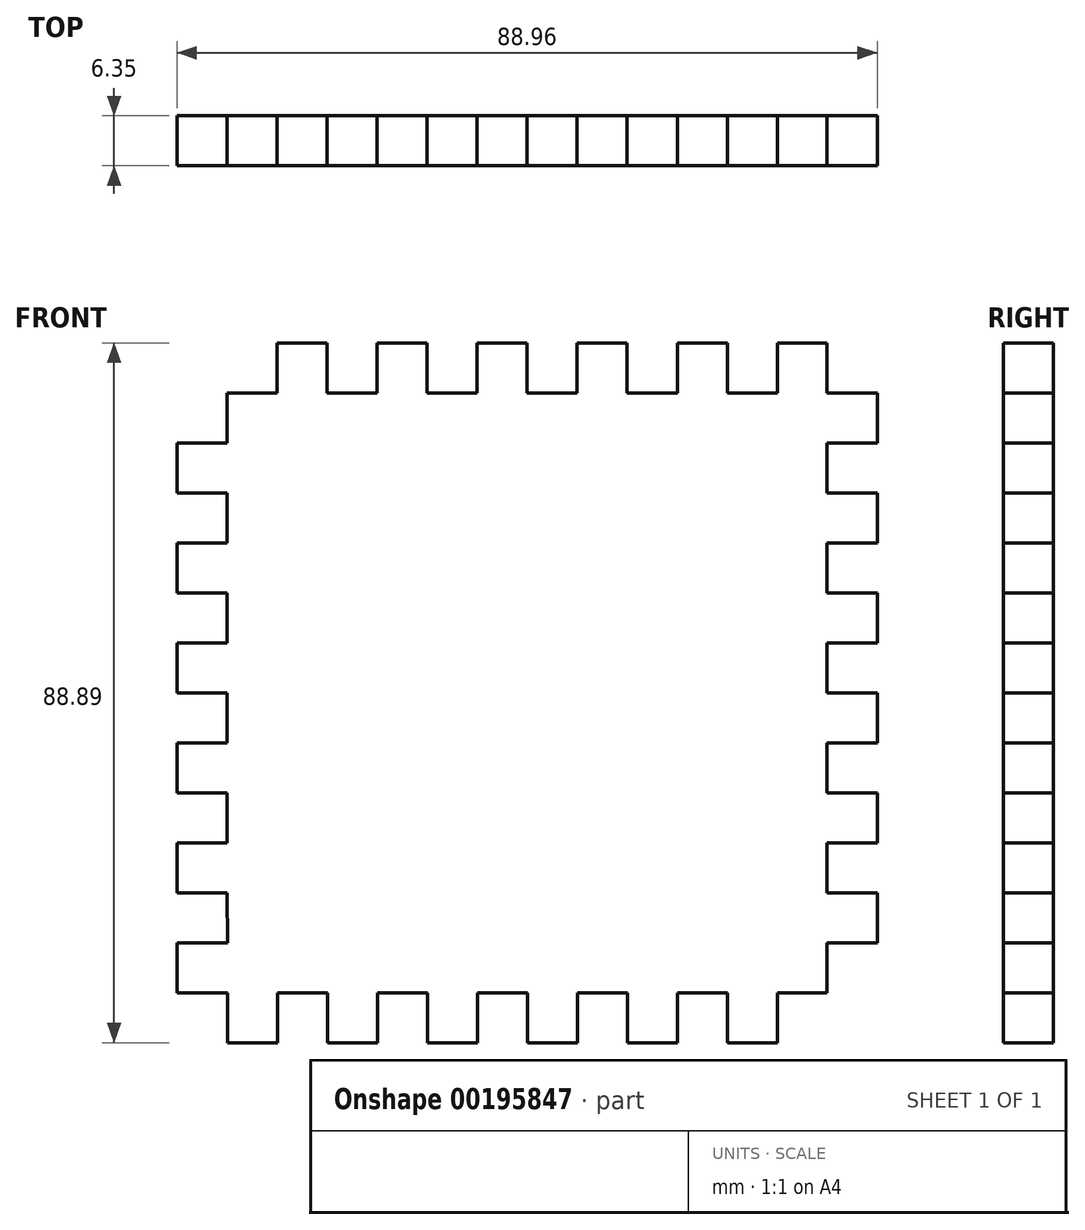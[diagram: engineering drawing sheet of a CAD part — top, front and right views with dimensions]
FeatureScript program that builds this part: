
annotation { "Feature Type Name" : "Feature", "Feature Type Description" : "" }
export const myFeature = defineFeature(function(context is Context, id is Id, definition is map)
    precondition{}
    {
        {
            var Q0;
            Q0=qCreatedBy(makeId("Front.planeOp"),FACE);
            var sketch = newSketch(context, id + "F0", { "sketchPlane" : qUnion([Q0])});
            skLineSegment(sketch, "E0.bottom", {"start": v(-31.75, 47.62) * mm, "end": v(-25.4, 47.62) * mm});
            skLineSegment(sketch, "E0.right", {"start": v(44.48, 41.27) * mm, "end": v(44.48, 34.93) * mm});
            skPoint(sketch, "E0.middle", {"position": v(0, 0) * mm});
            skLineSegment(sketch, "E1", {"start": v(-38.1, 41.27) * mm, "end": v(-31.75, 41.27) * mm});
            skLineSegment(sketch, "E2", {"start": v(-25.37, -41.27) * mm, "end": v(-25.32, -41.27) * mm});
            skLineSegment(sketch, "E3", {"start": v(-6.35, 41.27) * mm, "end": v(-6.35, 47.62) * mm});
            skLineSegment(sketch, "E4", {"start": v(-12.7, 47.62) * mm, "end": v(-19.05, 47.62) * mm});
            skLineSegment(sketch, "E5", {"start": v(0, 41.27) * mm, "end": v(0, 47.62) * mm});
            skLineSegment(sketch, "E6", {"start": v(6.35, 47.62) * mm, "end": v(6.35, 41.27) * mm});
            skLineSegment(sketch, "E7", {"start": v(12.7, 41.27) * mm, "end": v(12.7, 47.62) * mm});
            skLineSegment(sketch, "E8", {"start": v(6.35, 47.62) * mm, "end": v(12.7, 47.62) * mm});
            skLineSegment(sketch, "E9", {"start": v(0, 41.27) * mm, "end": v(6.35, 41.27) * mm});
            skLineSegment(sketch, "E10", {"start": v(19.08, 41.27) * mm, "end": v(19.08, 47.62) * mm});
            skLineSegment(sketch, "E11", {"start": v(19.08, 47.62) * mm, "end": v(25.43, 47.62) * mm});
            skLineSegment(sketch, "E12", {"start": v(25.43, 47.62) * mm, "end": v(25.43, 41.27) * mm});
            skLineSegment(sketch, "E13", {"start": v(25.43, 41.27) * mm, "end": v(31.78, 41.27) * mm});
            skLineSegment(sketch, "E14", {"start": v(31.78, 47.62) * mm, "end": v(31.78, 41.27) * mm});
            skLineSegment(sketch, "E15", {"start": v(31.78, 47.62) * mm, "end": v(31.78, 47.62) * mm});
            skLineSegment(sketch, "E16", {"start": v(-12.7, 47.62) * mm, "end": v(-12.7, 41.27) * mm});
            skLineSegment(sketch, "E17", {"start": v(-19.05, 47.62) * mm, "end": v(-19.05, 41.27) * mm});
            skLineSegment(sketch, "E18", {"start": v(-25.4, 47.62) * mm, "end": v(-25.4, 41.27) * mm});
            skLineSegment(sketch, "E19", {"start": v(-31.75, 47.62) * mm, "end": v(-31.75, 41.27) * mm});
            skLineSegment(sketch, "E20.trimOffspring", {"start": v(31.78, 47.62) * mm, "end": v(38.1, 47.62) * mm});
            skLineSegment(sketch, "E21.trimOffspring", {"start": v(-25.4, 47.62) * mm, "end": v(-31.75, 47.62) * mm});
            skLineSegment(sketch, "E22.trimOffspring", {"start": v(-6.35, 47.62) * mm, "end": v(0, 47.62) * mm});
            skLineSegment(sketch, "E23.trimOffspring", {"start": v(-19.05, 47.62) * mm, "end": v(-12.7, 47.62) * mm});
            skLineSegment(sketch, "E24.trimOffspring", {"start": v(38.1, 41.27) * mm, "end": v(44.48, 41.27) * mm});
            skLineSegment(sketch, "E25.trimOffspring", {"start": v(12.7, 41.27) * mm, "end": v(19.08, 41.27) * mm});
            skLineSegment(sketch, "E26.trimOffspring", {"start": v(-12.7, 41.27) * mm, "end": v(-6.35, 41.27) * mm});
            skLineSegment(sketch, "E27.trimOffspring", {"start": v(-25.4, 41.27) * mm, "end": v(-19.05, 41.27) * mm});
            skLineSegment(sketch, "E28", {"start": v(-44.48, 34.92) * mm, "end": v(-38.1, 34.92) * mm});
            skLineSegment(sketch, "E29", {"start": v(-44.48, 28.57) * mm, "end": v(-38.1, 28.57) * mm});
            skLineSegment(sketch, "E30", {"start": v(-44.48, 22.22) * mm, "end": v(-38.1, 22.22) * mm});
            skLineSegment(sketch, "E31", {"start": v(-44.48, 15.87) * mm, "end": v(-38.1, 15.87) * mm});
            skLineSegment(sketch, "E32", {"start": v(-44.48, 9.52) * mm, "end": v(-38.1, 9.52) * mm});
            skLineSegment(sketch, "E33", {"start": v(-44.48, 3.17) * mm, "end": v(-38.1, 3.17) * mm});
            skLineSegment(sketch, "E34", {"start": v(-44.48, -3.18) * mm, "end": v(-38.1, -3.18) * mm});
            skLineSegment(sketch, "E35", {"start": v(-44.48, -9.53) * mm, "end": v(-38.1, -9.53) * mm});
            skLineSegment(sketch, "E36", {"start": v(-44.48, -15.88) * mm, "end": v(-38.1, -15.88) * mm});
            skLineSegment(sketch, "E37", {"start": v(-44.48, -22.23) * mm, "end": v(-38.1, -22.23) * mm});
            skLineSegment(sketch, "E38", {"start": v(-44.48, -28.58) * mm, "end": v(-38.07, -28.58) * mm});
            skLineSegment(sketch, "E39", {"start": v(-31.72, -41.27) * mm, "end": v(-31.72, -34.92) * mm});
            skLineSegment(sketch, "E40", {"start": v(-25.37, -34.92) * mm, "end": v(-25.37, -41.27) * mm});
            skLineSegment(sketch, "E41", {"start": v(-19.02, -34.92) * mm, "end": v(-19.02, -41.27) * mm});
            skLineSegment(sketch, "E42", {"start": v(-12.67, -34.92) * mm, "end": v(-12.67, -41.28) * mm});
            skLineSegment(sketch, "E43", {"start": v(-6.32, -34.92) * mm, "end": v(-6.32, -41.28) * mm});
            skLineSegment(sketch, "E44", {"start": v(0.03, -34.92) * mm, "end": v(0.03, -41.27) * mm});
            skLineSegment(sketch, "E45", {"start": v(6.38, -34.92) * mm, "end": v(6.38, -41.27) * mm});
            skLineSegment(sketch, "E46", {"start": v(12.73, -34.92) * mm, "end": v(12.73, -41.27) * mm});
            skLineSegment(sketch, "E47", {"start": v(19.08, -34.92) * mm, "end": v(19.08, -41.27) * mm});
            skLineSegment(sketch, "E48", {"start": v(25.43, -34.92) * mm, "end": v(25.43, -41.27) * mm});
            skLineSegment(sketch, "E49", {"start": v(31.78, -34.92) * mm, "end": v(31.78, -41.27) * mm});
            skLineSegment(sketch, "E50", {"start": v(-12.67, -41.27) * mm, "end": v(-12.45, -41.27) * mm});
            skLineSegment(sketch, "E51", {"start": v(38.1, -28.57) * mm, "end": v(44.48, -28.57) * mm});
            skLineSegment(sketch, "E52", {"start": v(38.1, -22.22) * mm, "end": v(44.48, -22.22) * mm});
            skLineSegment(sketch, "E53", {"start": v(38.1, -15.87) * mm, "end": v(44.48, -15.87) * mm});
            skLineSegment(sketch, "E54", {"start": v(38.1, -9.52) * mm, "end": v(44.48, -9.52) * mm});
            skLineSegment(sketch, "E55", {"start": v(38.1, -3.17) * mm, "end": v(44.48, -3.17) * mm});
            skLineSegment(sketch, "E56", {"start": v(38.1, 3.18) * mm, "end": v(44.48, 3.18) * mm});
            skLineSegment(sketch, "E57", {"start": v(38.1, 9.53) * mm, "end": v(44.48, 9.53) * mm});
            skLineSegment(sketch, "E58", {"start": v(38.1, 15.88) * mm, "end": v(44.48, 15.88) * mm});
            skLineSegment(sketch, "E59", {"start": v(38.1, 22.23) * mm, "end": v(44.48, 22.23) * mm});
            skLineSegment(sketch, "E60", {"start": v(38.1, 28.58) * mm, "end": v(44.48, 28.58) * mm});
            skLineSegment(sketch, "E61", {"start": v(38.1, 34.93) * mm, "end": v(44.48, 34.93) * mm});
            skLineSegment(sketch, "E62.trimOffspring", {"start": v(44.48, -22.23) * mm, "end": v(44.48, -28.57) * mm});
            skLineSegment(sketch, "E63.trimOffspring", {"start": v(44.48, -9.52) * mm, "end": v(44.48, -15.88) * mm});
            skLineSegment(sketch, "E64.trimOffspring", {"start": v(44.48, 3.18) * mm, "end": v(44.48, -3.17) * mm});
            skLineSegment(sketch, "E65.trimOffspring", {"start": v(44.48, 15.88) * mm, "end": v(44.48, 9.53) * mm});
            skLineSegment(sketch, "E66.trimOffspring", {"start": v(44.48, 28.58) * mm, "end": v(44.48, 22.23) * mm});
            skLineSegment(sketch, "E67.trimOffspring", {"start": v(38.1, 34.93) * mm, "end": v(38.1, 28.58) * mm});
            skLineSegment(sketch, "E68.trimOffspring", {"start": v(38.1, 9.53) * mm, "end": v(38.1, 3.18) * mm});
            skLineSegment(sketch, "E69.trimOffspring", {"start": v(38.1, -3.17) * mm, "end": v(38.1, -9.52) * mm});
            skLineSegment(sketch, "E70.trimOffspring", {"start": v(38.1, -15.87) * mm, "end": v(38.1, -22.23) * mm});
            skLineSegment(sketch, "E71", {"start": v(38.1, 41.27) * mm, "end": v(38.1, 47.63) * mm});
            skLineSegment(sketch, "E72", {"start": v(38.1, 22.23) * mm, "end": v(38.1, 15.88) * mm});
            skLineSegment(sketch, "E73", {"start": v(38.1, -28.57) * mm, "end": v(38.1, -34.92) * mm});
            skLineSegment(sketch, "E74", {"start": v(-38.07, -34.93) * mm, "end": v(-38.07, -41.27) * mm});
            skLineSegment(sketch, "E75", {"start": v(-31.72, -34.92) * mm, "end": v(-25.37, -34.92) * mm});
            skLineSegment(sketch, "E76", {"start": v(-38.07, -41.27) * mm, "end": v(-31.72, -41.27) * mm});
            skLineSegment(sketch, "E77", {"start": v(-25.32, -41.27) * mm, "end": v(-19.02, -41.27) * mm});
            skLineSegment(sketch, "E78", {"start": v(0.03, -41.27) * mm, "end": v(6.38, -41.27) * mm});
            skLineSegment(sketch, "E79", {"start": v(12.73, -41.27) * mm, "end": v(19.08, -41.27) * mm});
            skLineSegment(sketch, "E80", {"start": v(25.43, -41.27) * mm, "end": v(31.78, -41.27) * mm});
            skLineSegment(sketch, "E81", {"start": v(-12.67, -41.28) * mm, "end": v(-6.32, -41.28) * mm});
            skLineSegment(sketch, "E82.trimOffspring", {"start": v(-6.32, -34.92) * mm, "end": v(0.03, -34.92) * mm});
            skLineSegment(sketch, "E83.trimOffspring", {"start": v(-19.02, -34.92) * mm, "end": v(-12.67, -34.92) * mm});
            skLineSegment(sketch, "E84.trimOffspring", {"start": v(6.38, -34.92) * mm, "end": v(12.73, -34.92) * mm});
            skLineSegment(sketch, "E85.trimOffspring", {"start": v(19.08, -34.92) * mm, "end": v(25.43, -34.92) * mm});
            skLineSegment(sketch, "E86.trimOffspring", {"start": v(31.78, -34.92) * mm, "end": v(38.1, -34.92) * mm});
            skLineSegment(sketch, "E87", {"start": v(-44.48, 34.92) * mm, "end": v(-44.48, 28.57) * mm});
            skLineSegment(sketch, "E88", {"start": v(-44.48, -34.92) * mm, "end": v(-38.07, -34.92) * mm});
            skLineSegment(sketch, "E89.trimOffspring", {"start": v(-44.48, -28.58) * mm, "end": v(-44.48, -34.93) * mm});
            skLineSegment(sketch, "E90.trimOffspring", {"start": v(-44.48, -15.88) * mm, "end": v(-44.48, -22.23) * mm});
            skLineSegment(sketch, "E91.trimOffspring", {"start": v(-44.48, -3.18) * mm, "end": v(-44.48, -9.53) * mm});
            skLineSegment(sketch, "E92.trimOffspring", {"start": v(-44.48, 22.22) * mm, "end": v(-44.48, 15.87) * mm});
            skLineSegment(sketch, "E93.trimOffspring", {"start": v(-44.48, 9.52) * mm, "end": v(-44.48, 3.17) * mm});
            skLineSegment(sketch, "E94", {"start": v(-38.1, 41.27) * mm, "end": v(-38.1, 34.92) * mm});
            skLineSegment(sketch, "E95", {"start": v(-38.1, 28.57) * mm, "end": v(-38.1, 22.22) * mm});
            skLineSegment(sketch, "E96", {"start": v(-38.1, 15.87) * mm, "end": v(-38.1, 9.52) * mm});
            skLineSegment(sketch, "E97", {"start": v(-38.1, 3.17) * mm, "end": v(-38.1, -3.18) * mm});
            skLineSegment(sketch, "E98", {"start": v(-38.1, -9.53) * mm, "end": v(-38.1, -15.88) * mm});
            skLineSegment(sketch, "E99", {"start": v(-38.1, -22.23) * mm, "end": v(-38.07, -28.58) * mm});
            skPoint(sketch, "E100.orphan", {"position": v(-38.1, 34.92) * mm});
            skSolve(sketch);
        }
        {
            var Q0;
            Q0 = qSketchRegion(id + "F0", true);
            extrude(context, id + "F1", {"entities" : qUnion([Q0]), "depth" : 6.35 * mm});
        }
    });
